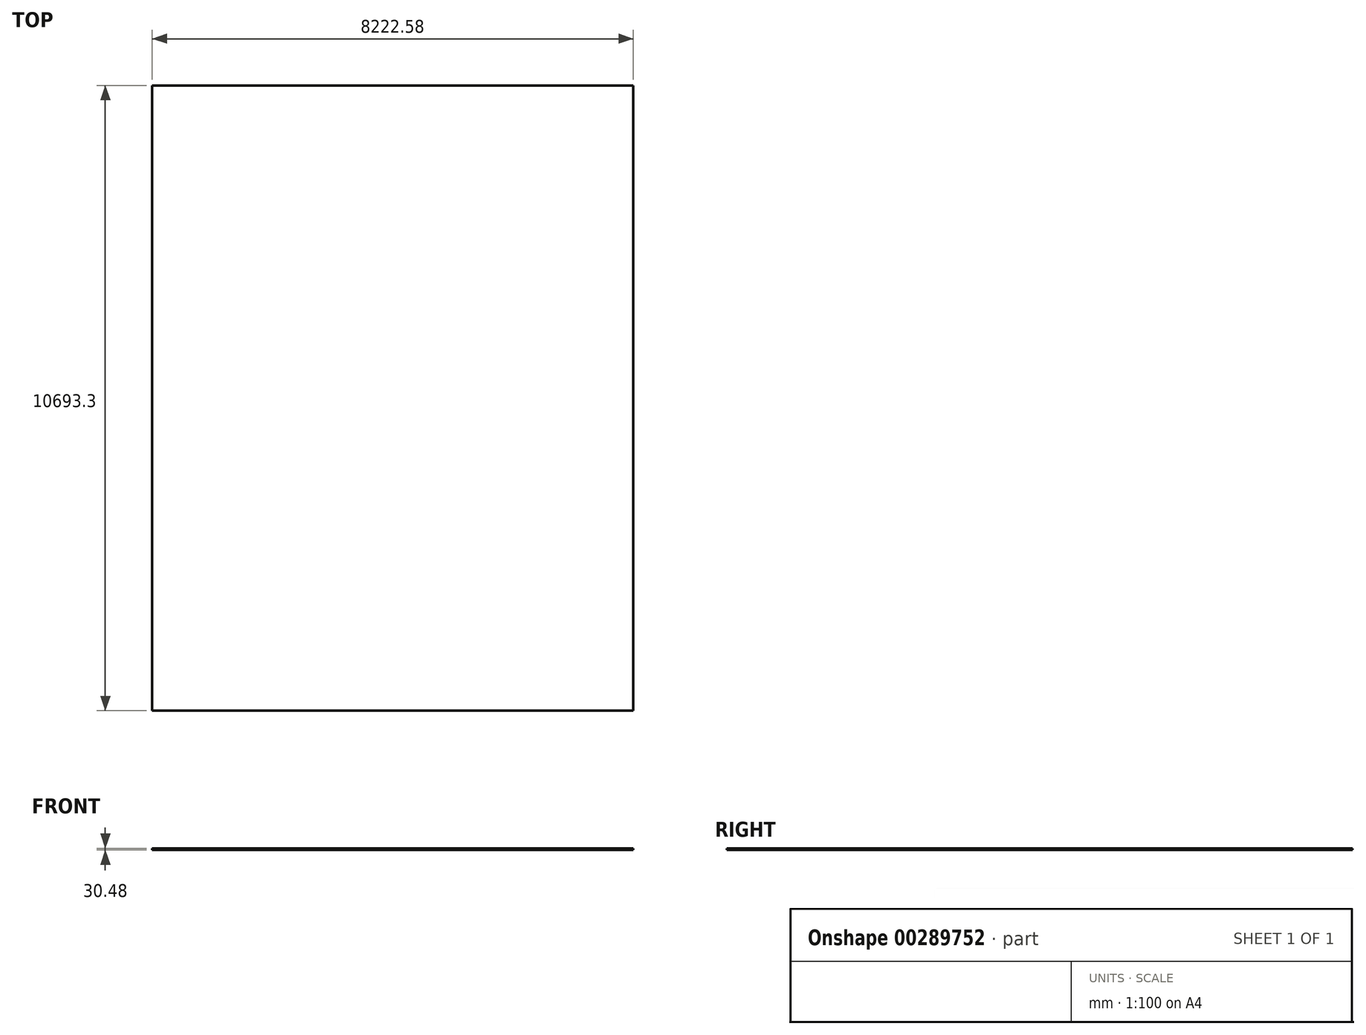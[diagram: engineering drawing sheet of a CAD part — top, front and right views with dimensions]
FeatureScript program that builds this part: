
annotation { "Feature Type Name" : "Feature", "Feature Type Description" : "" }
export const myFeature = defineFeature(function(context is Context, id is Id, definition is map)
    precondition{}
    {
        {
            var Q0;
            Q0=qCreatedBy(makeId("Top.planeOp"),FACE);
            var sketch = newSketch(context, id + "F0", { "sketchPlane" : qUnion([Q0])});
            skLineSegment(sketch, "E0.bottom", {"start": v(4111.3, -5346.65) * mm, "end": v(-4111.3, -5346.65) * mm});
            skLineSegment(sketch, "E0.top", {"start": v(4111.3, 5346.65) * mm, "end": v(-4111.3, 5346.65) * mm});
            skLineSegment(sketch, "E0.left", {"start": v(4111.3, -5346.65) * mm, "end": v(4111.3, 5346.65) * mm});
            skLineSegment(sketch, "E0.right", {"start": v(-4111.3, -5346.65) * mm, "end": v(-4111.3, 5346.65) * mm});
            skPoint(sketch, "E0.middle", {"position": v(0, 0) * mm});
            skSolve(sketch);
        }
        {
            var Q0;
            Q0=makeQuery(id+"F0.imprint","IMPRINT",FACE,{"disambiguationData":[TD([[makeQuery(id+"F0.imprint","IMPRINT",EDGE,{"derivedFrom":sQuery(id+"F0.wireOp",EDGE,"E0.bottom")}),-1.0]])]});
            extrude(context, id + "F1", {"entities" : qUnion([Q0]), "depth" : 30.48 * mm});
        }
    });
